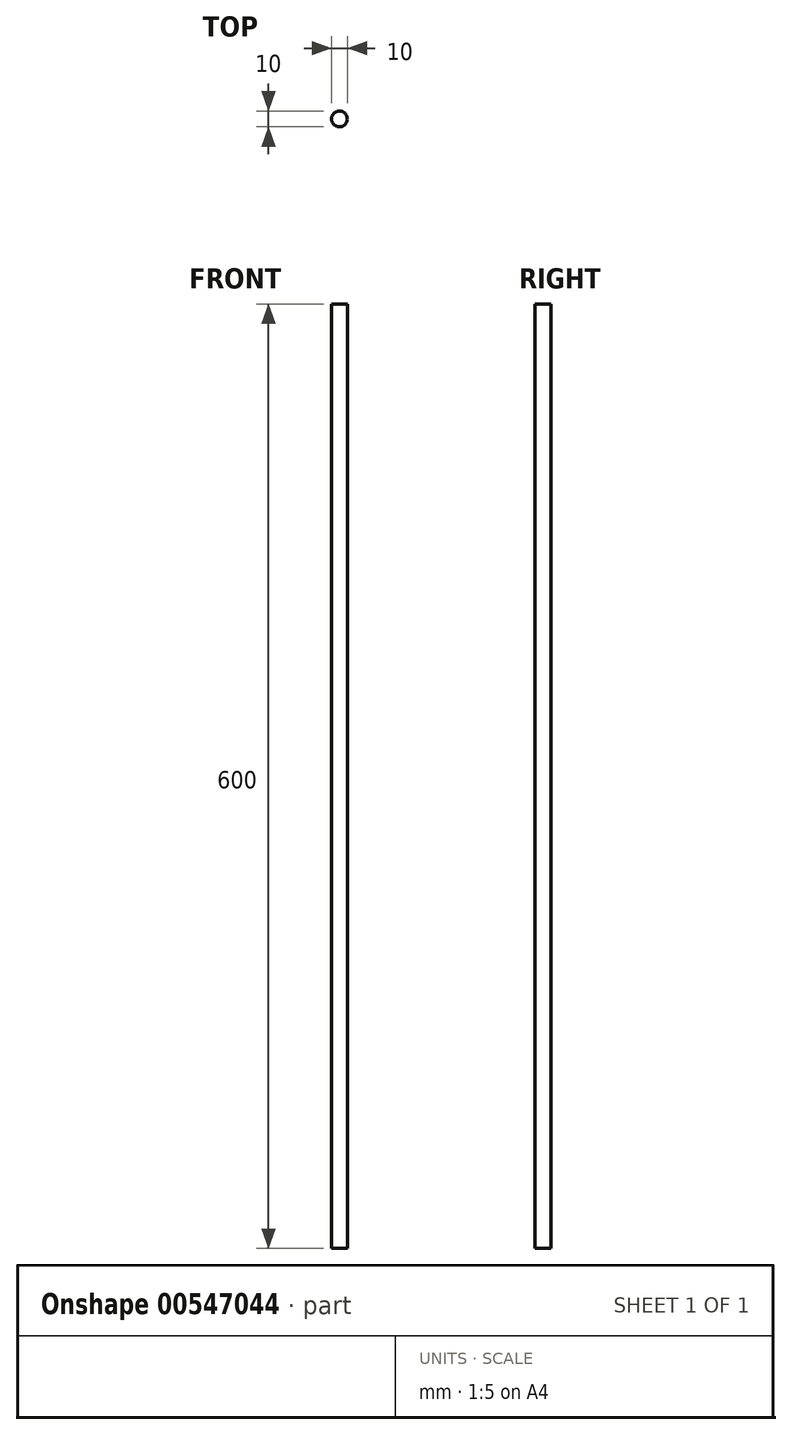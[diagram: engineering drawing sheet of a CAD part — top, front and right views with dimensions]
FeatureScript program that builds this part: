
annotation { "Feature Type Name" : "Feature", "Feature Type Description" : "" }
export const myFeature = defineFeature(function(context is Context, id is Id, definition is map)
    precondition{}
    {
        {
            var Q0;
            Q0=qCreatedBy(makeId("Top.planeOp"),FACE);
            var sketch = newSketch(context, id + "F0", { "sketchPlane" : qUnion([Q0])});
            skCircle(sketch, "E0", {"center": v(0, 0) * mm, "radius": 5 * mm});
            skSolve(sketch);
        }
        {
            var Q0;
            Q0=makeQuery(id+"F0.imprint","IMPRINT",FACE,{"disambiguationData":[TD([[makeQuery(id+"F0.imprint","IMPRINT",EDGE,{"derivedFrom":sQuery(id+"F0.wireOp",EDGE,"E0")}),1.0]])]});
            extrude(context, id + "F1", {"entities" : qUnion([Q0]), "depth" : 600 * mm, "offsetDistance" : 25 * mm});
        }
    });
